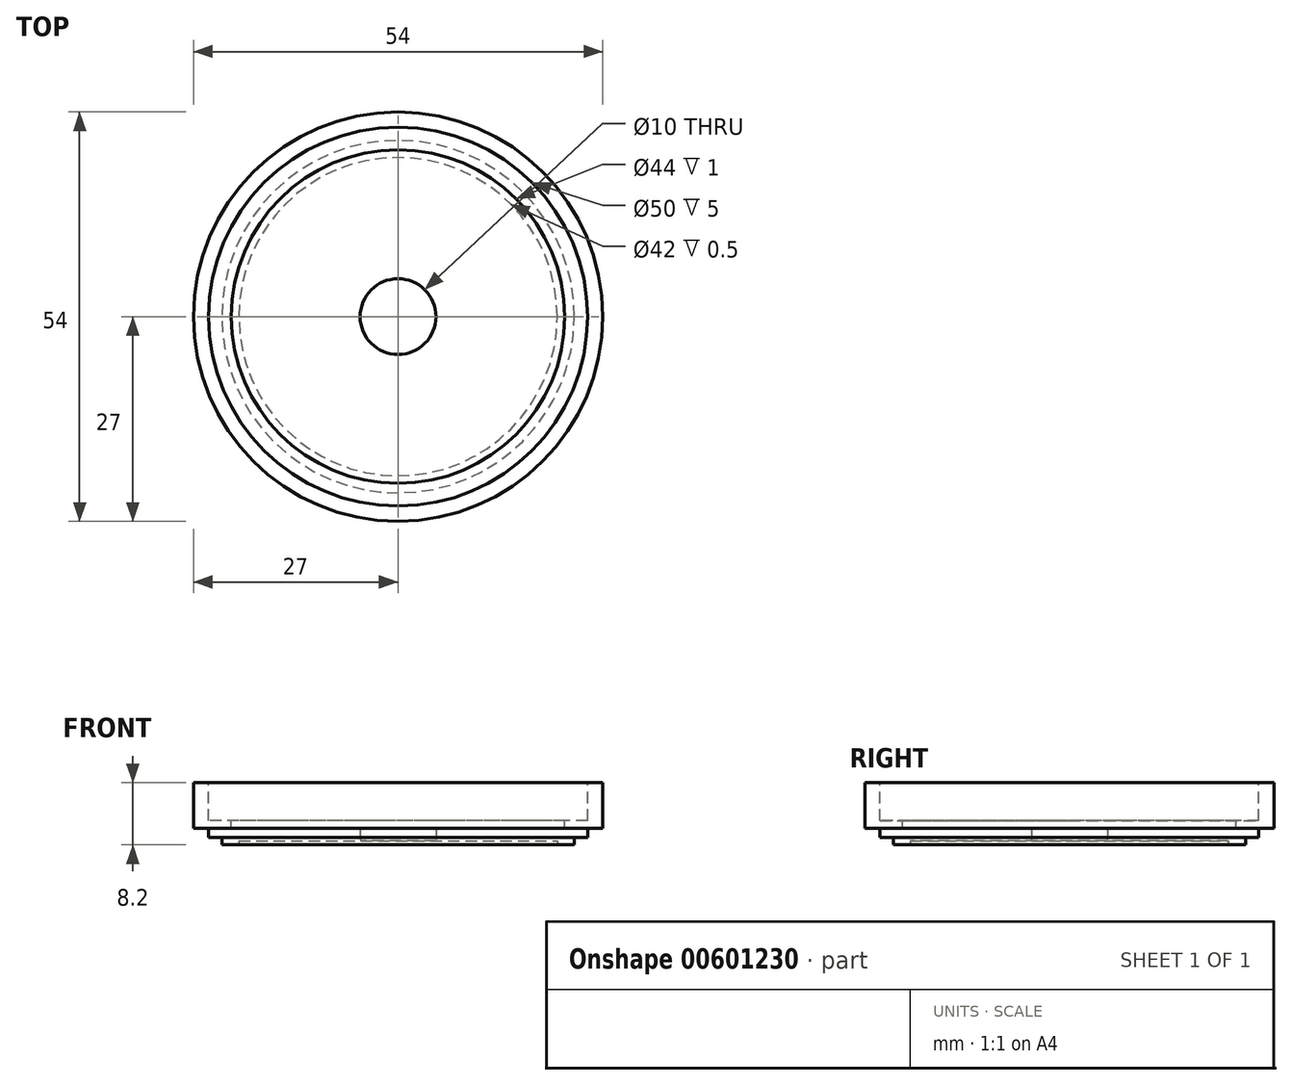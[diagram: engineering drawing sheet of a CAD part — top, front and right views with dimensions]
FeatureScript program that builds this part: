
annotation { "Feature Type Name" : "Feature", "Feature Type Description" : "" }
export const myFeature = defineFeature(function(context is Context, id is Id, definition is map)
    precondition{}
    {
        {
            var Q0;
            Q0=qCreatedBy(makeId("Top.planeOp"),FACE);
            var sketch = newSketch(context, id + "F0", { "sketchPlane" : qUnion([Q0])});
            skCircle(sketch, "E0", {"center": v(0, 0) * mm, "radius": 23.25 * mm});
            skCircle(sketch, "E1", {"center": v(0, 0) * mm, "radius": 5 * mm});
            skSolve(sketch);
        }
        {
            var Q0;
            Q0=makeQuery(id+"F0.imprint","IMPRINT",FACE,{"disambiguationData":[TD([[makeQuery(id+"F0.imprint","IMPRINT",EDGE,{"derivedFrom":sQuery(id+"F0.wireOp",EDGE,"E0")}),1.0]])]});
            extrude(context, id + "F1", {"entities" : qUnion([Q0]), "depth" : 1 * mm, "offsetDistance" : 25 * mm});
        }
        {
            var Q0;
            Q0=makeQuery(id+"F1.opExtrude","CAP_FACE",FACE,{"disambiguationData":[OSD([sQuery(id+"F0.wireOp",EDGE,"E0"),sQuery(id+"F0.wireOp",EDGE,"E1")])],"isStart":false});
            var sketch = newSketch(context, id + "F2", { "sketchPlane" : qUnion([Q0])});
            skCircle(sketch, "E2", {"center": v(0, 0) * mm, "radius": 25 * mm});
            skSolve(sketch);
        }
        {
            var Q0;
            Q0=makeQuery(id+"F2.imprint","IMPRINT",FACE,{"disambiguationData":[TD([[makeQuery(id+"F2.imprint","IMPRINT",EDGE,{"derivedFrom":sQuery(id+"F2.wireOp",EDGE,"E2")}),1.0]])]});
            var Q1;
            Q1=makeQuery(id+"F2.imprint","IMPRINT",FACE,{"disambiguationData":[TD([[makeQuery(id+"F2.imprint","IMPRINT",EDGE,{"derivedFrom":makeQuery(id+"F1.opExtrude","CAP_EDGE",EDGE,{"disambiguationData":[OSD([sQuery(id+"F0.wireOp",EDGE,"E0")])],"isStart":false})}),1.0]])]});
            extrude(context, id + "F3", {"entities" : qUnion([Q0, Q1]), "operationType" : NewBodyOperationType.ADD, "depth" : 1.2 * mm, "offsetDistance" : 25 * mm});
        }
        {
            var Q0;
            Q0=makeQuery(id+"F3.opExtrude","CAP_FACE",FACE,{"disambiguationData":[OSD([sQuery(id+"F0.wireOp",EDGE,"E1"),sQuery(id+"F2.wireOp",EDGE,"E2")])],"isStart":false});
            var sketch = newSketch(context, id + "F4", { "sketchPlane" : qUnion([Q0])});
            skCircle(sketch, "E3", {"center": v(0, 0) * mm, "radius": 27 * mm});
            skSolve(sketch);
        }
        {
            var Q0;
            Q0=makeQuery(id+"F4.imprint","IMPRINT",FACE,{"disambiguationData":[TD([[makeQuery(id+"F4.imprint","IMPRINT",EDGE,{"derivedFrom":sQuery(id+"F4.wireOp",EDGE,"E3")}),1.0]])]});
            var Q1;
            Q1=makeQuery(id+"F4.imprint","IMPRINT",FACE,{"disambiguationData":[TD([[makeQuery(id+"F4.imprint","IMPRINT",EDGE,{"derivedFrom":makeQuery(id+"F3.opExtrude","CAP_EDGE",EDGE,{"disambiguationData":[OSD([sQuery(id+"F2.wireOp",EDGE,"E2")])],"isStart":false})}),1.0]])]});
            extrude(context, id + "F5", {"entities" : qUnion([Q0, Q1]), "operationType" : NewBodyOperationType.ADD, "depth" : 6 * mm, "offsetDistance" : 25 * mm});
        }
        {
            var Q0;
            Q0=makeQuery(id+"F5.opExtrude","CAP_FACE",FACE,{"disambiguationData":[OSD([sQuery(id+"F0.wireOp",EDGE,"E1"),sQuery(id+"F4.wireOp",EDGE,"E3")])],"isStart":false});
            var sketch = newSketch(context, id + "F6", { "sketchPlane" : qUnion([Q0])});
            skCircle(sketch, "E4", {"center": v(0, 0) * mm, "radius": 22 * mm});
            skSolve(sketch);
        }
        {
            var Q0;
            Q0=makeQuery(id+"F6.imprint","IMPRINT",FACE,{"disambiguationData":[TD([[makeQuery(id+"F6.imprint","IMPRINT",EDGE,{"derivedFrom":sQuery(id+"F6.wireOp",EDGE,"E4")}),1.0]])]});
            extrude(context, id + "F7", {"entities" : qUnion([Q0]), "operationType" : NewBodyOperationType.REMOVE, "oppositeDirection" : true, "depth" : 6 * mm, "offsetDistance" : 25 * mm});
        }
        {
            var Q0;
            Q0=makeQuery(id+"F5.opExtrude","CAP_FACE",FACE,{"disambiguationData":[OSD([sQuery(id+"F0.wireOp",EDGE,"E1"),sQuery(id+"F4.wireOp",EDGE,"E3")])],"isStart":false});
            var sketch = newSketch(context, id + "F8", { "sketchPlane" : qUnion([Q0])});
            skCircle(sketch, "E5", {"center": v(0, 0) * mm, "radius": 25 * mm});
            skSolve(sketch);
        }
        {
            var Q0;
            Q0=makeQuery(id+"F8.imprint","IMPRINT",FACE,{"disambiguationData":[TD([[makeQuery(id+"F8.imprint","IMPRINT",EDGE,{"derivedFrom":sQuery(id+"F8.wireOp",EDGE,"E5")}),1.0]])]});
            extrude(context, id + "F9", {"entities" : qUnion([Q0]), "operationType" : NewBodyOperationType.REMOVE, "oppositeDirection" : true, "depth" : 5 * mm, "offsetDistance" : 25 * mm});
        }
        {
            var Q0;
            Q0=makeQuery(id+"F1.opExtrude","CAP_FACE",FACE,{"disambiguationData":[OSD([sQuery(id+"F0.wireOp",EDGE,"E0"),sQuery(id+"F0.wireOp",EDGE,"E1")])],"isStart":true});
            var sketch = newSketch(context, id + "F10", { "sketchPlane" : qUnion([Q0])});
            skCircle(sketch, "E6", {"center": v(0, 0) * mm, "radius": 21 * mm});
            skSolve(sketch);
        }
        {
            var Q0;
            Q0=makeQuery(id+"F10.imprint","IMPRINT",FACE,{"disambiguationData":[TD([[makeQuery(id+"F10.imprint","IMPRINT",EDGE,{"derivedFrom":sQuery(id+"F10.wireOp",EDGE,"E6")}),1.0]])]});
            extrude(context, id + "F11", {"entities" : qUnion([Q0]), "operationType" : NewBodyOperationType.REMOVE, "oppositeDirection" : true, "depth" : 0.5 * mm, "offsetDistance" : 25 * mm});
        }
    });
